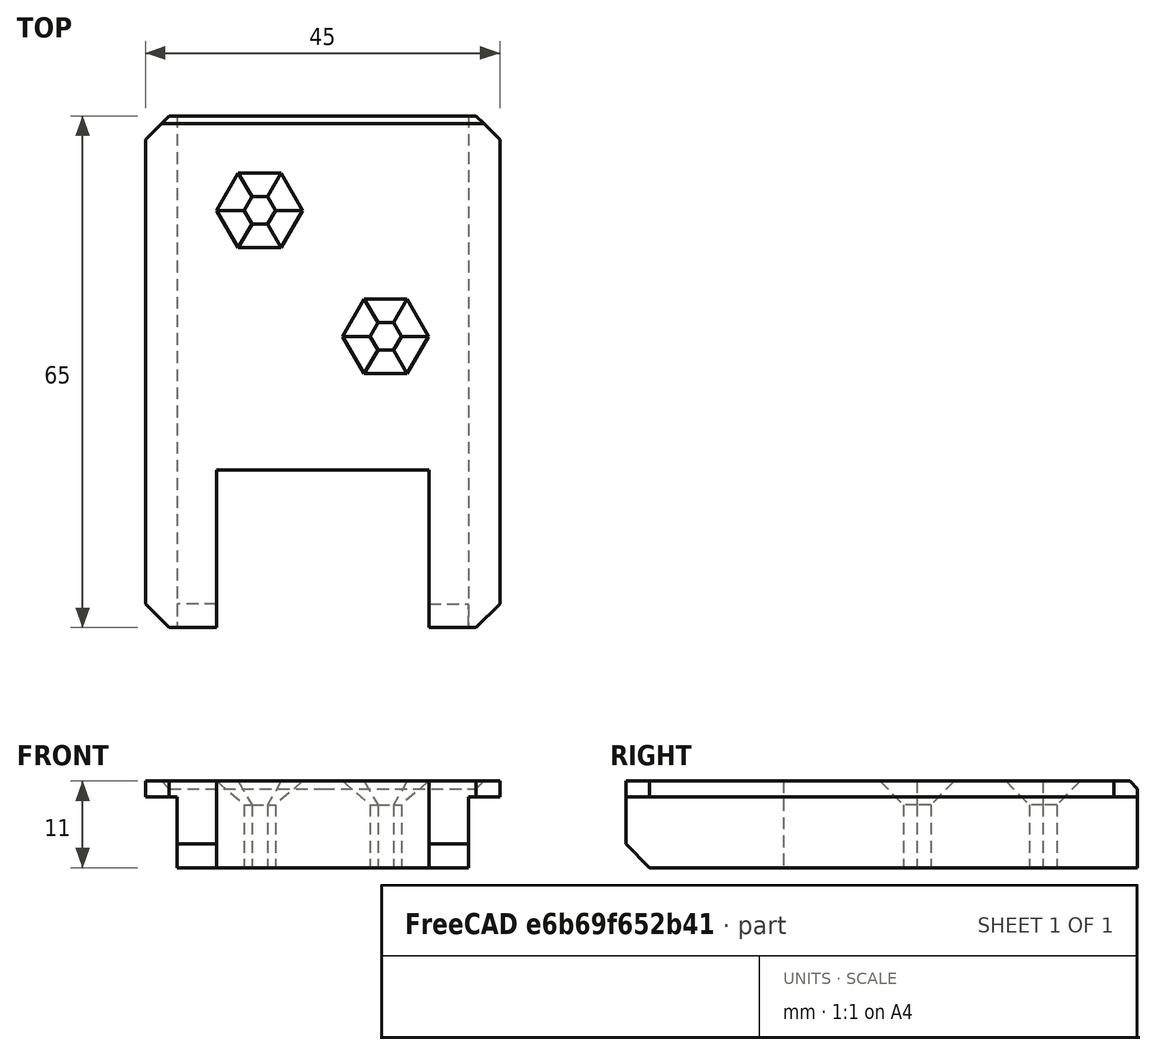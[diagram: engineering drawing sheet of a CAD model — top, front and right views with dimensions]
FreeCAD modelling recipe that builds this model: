
FCSTD DOCUMENT  (FreeCAD 0.19R)
Label: milwakeeholder
License: All rights reserved
LicenseURL: http://en.wikipedia.org/wiki/All_rights_reserved
objects: PartDesign::Chamfer×5, Sketcher::SketchObject×3, PartDesign::Pocket×2, PartDesign::Pad×1, PartDesign::Mirrored×1, PartDesign::Body×1, Mesh::Feature×1
note: 21 computed .brp shape members not serialized (recipe doc carries the construction recipe); baked Part::Feature solids carry a one-line shape summary decoded from their .brp

FEATURE [Sketcher::SketchObject] Sketch
  FullyConstrained = true
  MapMode = 5
  Placement = pos=(0,0,0) rot=(1,0,0;1.5708rad)
  Support = -> [XZ_Plane]
  sketch-geometry (6):
    g0: LineSegment StartX=18.5 StartY=0 StartZ=0 EndX=18.5 EndY=9 EndZ=0
    g1: LineSegment StartX=18.5 StartY=9 StartZ=0 EndX=22.5 EndY=9 EndZ=0
    g2: LineSegment StartX=22.5 StartY=9 StartZ=0 EndX=22.5 EndY=11 EndZ=0
    g3: LineSegment StartX=22.5 StartY=11 StartZ=0 EndX=0 EndY=11 EndZ=0
    g4: LineSegment StartX=0 StartY=11 StartZ=0 EndX=0 EndY=0 EndZ=0
    g5: LineSegment StartX=0 StartY=0 StartZ=0 EndX=18.5 EndY=0 EndZ=0
  constraints (17):
    c: PointOnObject(g0,g-1)
    c: Coincident(g0,g1)
    c: Horizontal(g1)
    c: Coincident(g1,g2)
    c: Vertical(g2)
    c: Vertical(g0)
    c: DistanceX(g0) = 18.5
    c: Distance(g0) = 9
    c: Distance(g1) = 4
    c: Distance(g2) = 2
    c: Coincident(g2,g3)
    c: Horizontal(g3)
    c: Coincident(g3,g4)
    c: Coincident(g4,g-1)
    c: Vertical(g4)
    c: Coincident(g4,g5)
    c: Coincident(g5,g0)
FEATURE [PartDesign::Pad] Pad
  Direction = (1,1,1)
  Length = 65
  Length2 = 100
  Placement = pos=(0,0,0) rot=(1,0,0;1.5708rad)
  Profile = -> Sketch
  Type = 0
FEATURE [PartDesign::Mirrored] Mirrored
  BaseFeature = -> Pad
  MirrorPlane = -> Sketch [V_Axis]
  Originals = -> [Pad]
  Placement = pos=(0,0,0) rot=(1,0,0;1.5708rad)
FEATURE [Sketcher::SketchObject] Sketch001
  FullyConstrained = false
  MapMode = 5
  Placement = pos=(0,2.4e-15,11) rot=(0,0,1;3.14159rad)
  Support = -> [Mirrored]
  sketch-geometry (4):
    g0: LineSegment StartX=-13.5 StartY=81.8654 StartZ=0 EndX=13.5 EndY=81.8654 EndZ=0
    g1: LineSegment StartX=13.5 StartY=81.8654 StartZ=0 EndX=13.5 EndY=45 EndZ=0
    g2: LineSegment StartX=13.5 StartY=45 StartZ=0 EndX=-13.5 EndY=45 EndZ=0
    g3: LineSegment StartX=-13.5 StartY=45 StartZ=0 EndX=-13.5 EndY=81.8654 EndZ=0
  constraints (10):
    c: Coincident(g0,g1)
    c: Coincident(g1,g2)
    c: Coincident(g2,g3)
    c: Coincident(g3,g0)
    c: Horizontal(g2)
    c: Vertical(g1)
    c: Vertical(g3)
    c: Distance(g0) = 27
    c: Symmetric(g0,g0,g-2)
    c: DistanceY(g2) = 45
FEATURE [PartDesign::Pocket] Pocket
  BaseFeature = -> Mirrored
  Length = 5
  Length2 = 100
  Placement = pos=(0,0,0) rot=(1,0,0;1.5708rad)
  Profile = -> Sketch001
  Type = 1
FEATURE [PartDesign::Chamfer] Chamfer
  Angle = 45
  Base = -> Pocket [Edge33,Edge13]
  BaseFeature = -> Pocket
  ChamferType = 0
  FlipDirection = false
  Placement = pos=(0,0,0) rot=(1,0,0;1.5708rad)
  Size = 3
  Size2 = 1
  SupportTransform = false
FEATURE [PartDesign::Chamfer] Chamfer001
  Angle = 45
  Base = -> Chamfer [Edge30,Edge16]
  BaseFeature = -> Chamfer
  ChamferType = 0
  FlipDirection = false
  Placement = pos=(0,0,0) rot=(1,0,0;1.5708rad)
  Size = 1
  Size2 = 1
  SupportTransform = false
FEATURE [PartDesign::Chamfer] Chamfer002
  Angle = 45
  Base = -> Chamfer001 [Edge53,Edge21]
  BaseFeature = -> Chamfer001
  ChamferType = 0
  FlipDirection = false
  Placement = pos=(0,0,0) rot=(1,0,0;1.5708rad)
  Size = 3
  Size2 = 1
  SupportTransform = false
FEATURE [PartDesign::Chamfer] Chamfer003
  Angle = 45
  Base = -> Chamfer002 [Edge17,Edge49]
  BaseFeature = -> Chamfer002
  ChamferType = 0
  FlipDirection = false
  Placement = pos=(0,0,0) rot=(1,0,0;1.5708rad)
  Size = 3
  Size2 = 1
  SupportTransform = false
FEATURE [Sketcher::SketchObject] Sketch002
  FullyConstrained = true
  MapMode = 5
  Placement = pos=(0,1.22e-14,11) rot=(0,0,1;3.14159rad)
  Support = -> [Chamfer003]
  sketch-geometry (14):
    g0: LineSegment StartX=-7 StartY=26.2679 StartZ=0 EndX=-6 EndY=28 EndZ=0
    g1: LineSegment StartX=-6 StartY=28 StartZ=0 EndX=-7 EndY=29.7321 EndZ=0
    g2: LineSegment StartX=-7 StartY=29.7321 StartZ=0 EndX=-9 EndY=29.7321 EndZ=0
    g3: LineSegment StartX=-9 StartY=29.7321 StartZ=0 EndX=-10 EndY=28 EndZ=0
    g4: LineSegment StartX=-10 StartY=28 StartZ=0 EndX=-9 EndY=26.2679 EndZ=0
    g5: LineSegment StartX=-9 StartY=26.2679 StartZ=0 EndX=-7 EndY=26.2679 EndZ=0
    g6: Circle CenterX=-8 CenterY=28 CenterZ=0 NormalX=0 NormalY=0 NormalZ=1 AngleXU=0 Radius=2
    g7: LineSegment StartX=9 StartY=10.2679 StartZ=0 EndX=10 EndY=12 EndZ=0
    g8: LineSegment StartX=10 StartY=12 StartZ=0 EndX=9 EndY=13.7321 EndZ=0
    g9: LineSegment StartX=9 StartY=13.7321 StartZ=0 EndX=7 EndY=13.7321 EndZ=0
    g10: LineSegment StartX=7 StartY=13.7321 StartZ=0 EndX=6 EndY=12 EndZ=0
    g11: LineSegment StartX=6 StartY=12 StartZ=0 EndX=7 EndY=10.2679 EndZ=0
    g12: LineSegment StartX=7 StartY=10.2679 StartZ=0 EndX=9 EndY=10.2679 EndZ=0
    g13: Circle CenterX=8 CenterY=12 CenterZ=0 NormalX=0 NormalY=0 NormalZ=1 AngleXU=0 Radius=2
  constraints (34):
    c: Coincident(g0,g1)
    c: Coincident(g1,g2)
    c: Coincident(g2,g3)
    c: Coincident(g3,g4)
    c: Coincident(g4,g5)
    c: Coincident(g5,g0)
    c: Equal(g0, g1-g5) x5
    c: PointOnObject(g0,g6)
    c: PointOnObject(g1,g6)
    c: PointOnObject(g2,g6)
    c: PointOnObject(g3,g6)
    c: PointOnObject(g4,g6)
    c: PointOnObject(g5,g6)
    c: Coincident(g7,g8)
    c: Coincident(g8,g9)
    c: Coincident(g9,g10)
    c: Coincident(g10,g11)
    c: Coincident(g11,g12)
    c: Coincident(g12,g7)
    c: Equal(g7, g8-g12) x5
    c: PointOnObject(g7,g13)
    c: PointOnObject(g8,g13)
    c: PointOnObject(g9,g13)
    c: PointOnObject(g10,g13)
    c: PointOnObject(g11,g13)
    c: PointOnObject(g12,g13)
    c: Horizontal(g9)
    c: Horizontal(g2)
    c: Radius(g6) = 2
    c: Equal(g6,g13)
    c: DistanceX(g13) = 8
    c: DistanceX(g6) = -8
    c: DistanceY(g13) = 12
    c: DistanceY(g6) = 28
FEATURE [PartDesign::Pocket] Pocket001
  BaseFeature = -> Chamfer003
  Length = 5
  Length2 = 100
  Placement = pos=(0,0,0) rot=(1,0,0;1.5708rad)
  Profile = -> Sketch002
  Type = 1
FEATURE [PartDesign::Chamfer] Chamfer004
  Angle = 45
  Base = -> Pocket001 [Edge23,Edge22,Edge21,Edge20,Edge19,Edge24,Edge57,Edge58,Edge59,Edge60,Edge61,Edge56]
  BaseFeature = -> Pocket001
  ChamferType = 0
  FlipDirection = false
  Placement = pos=(0,0,0) rot=(1,0,0;1.5708rad)
  Size = 3
  Size2 = 1
  SupportTransform = false
FEATURE [PartDesign::Body] Body
  Group = -> [Sketch,Pad,Mirrored,Sketch001,Pocket,Chamfer,Chamfer001,Chamfer002,Chamfer003,Sketch002,Pocket001,Chamfer004]
  Origin = -> Origin
  Tip = -> Chamfer004
FEATURE [Mesh::Feature] Mesh  label="Chamfer004 (Meshed)"
